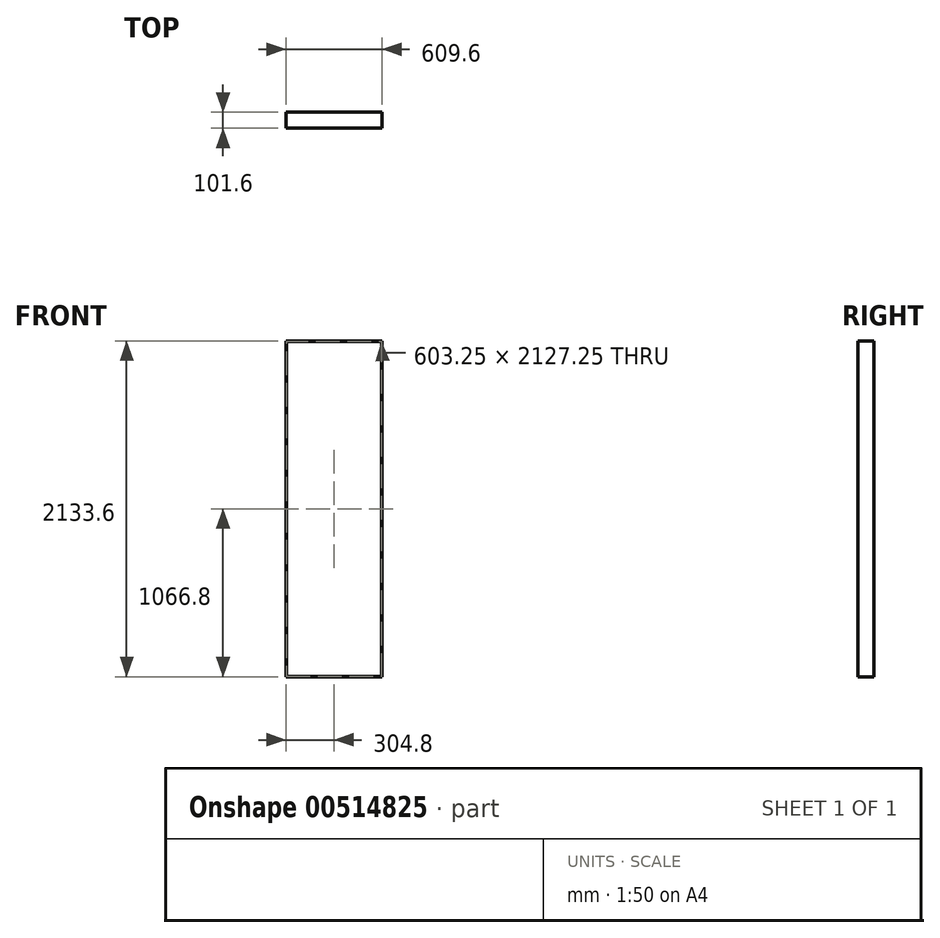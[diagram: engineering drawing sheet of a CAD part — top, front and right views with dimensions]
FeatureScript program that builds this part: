
annotation { "Feature Type Name" : "Feature", "Feature Type Description" : "" }
export const myFeature = defineFeature(function(context is Context, id is Id, definition is map)
    precondition{}
    {
        {
            var Q0;
            Q0=qCreatedBy(makeId("Front.planeOp"),FACE);
            var sketch = newSketch(context, id + "F0", { "sketchPlane" : qUnion([Q0])});
            skLineSegment(sketch, "E0.bottom", {"start": v(0, 0) * mm, "end": v(609.6, 0) * mm});
            skLineSegment(sketch, "E0.top", {"start": v(0, 2133.6) * mm, "end": v(609.6, 2133.6) * mm});
            skLineSegment(sketch, "E0.left", {"start": v(0, 0) * mm, "end": v(0, 2133.6) * mm});
            skLineSegment(sketch, "E0.right", {"start": v(609.6, 0) * mm, "end": v(609.6, 2133.6) * mm});
            skLineSegment(sketch, "E1.0", {"start": v(3.17, 3.18) * mm, "end": v(3.17, 2130.43) * mm});
            skLineSegment(sketch, "E1.1", {"start": v(3.18, 3.18) * mm, "end": v(606.43, 3.18) * mm});
            skLineSegment(sketch, "E1.2", {"start": v(606.43, 3.18) * mm, "end": v(606.42, 2130.43) * mm});
            skLineSegment(sketch, "E1.3", {"start": v(3.17, 2130.43) * mm, "end": v(606.42, 2130.43) * mm});
            skSolve(sketch);
        }
        {
            var Q0;
            Q0=makeQuery(id+"F0.imprint","IMPRINT",FACE,{"disambiguationData":[TD([[makeQuery(id+"F0.imprint","IMPRINT",EDGE,{"derivedFrom":sQuery(id+"F0.wireOp",EDGE,"E0.bottom")}),1.0]])]});
            extrude(context, id + "F1", {"entities" : qUnion([Q0]), "depth" : 101.6 * mm, "offsetDistance" : 25.4 * mm});
        }
    });
